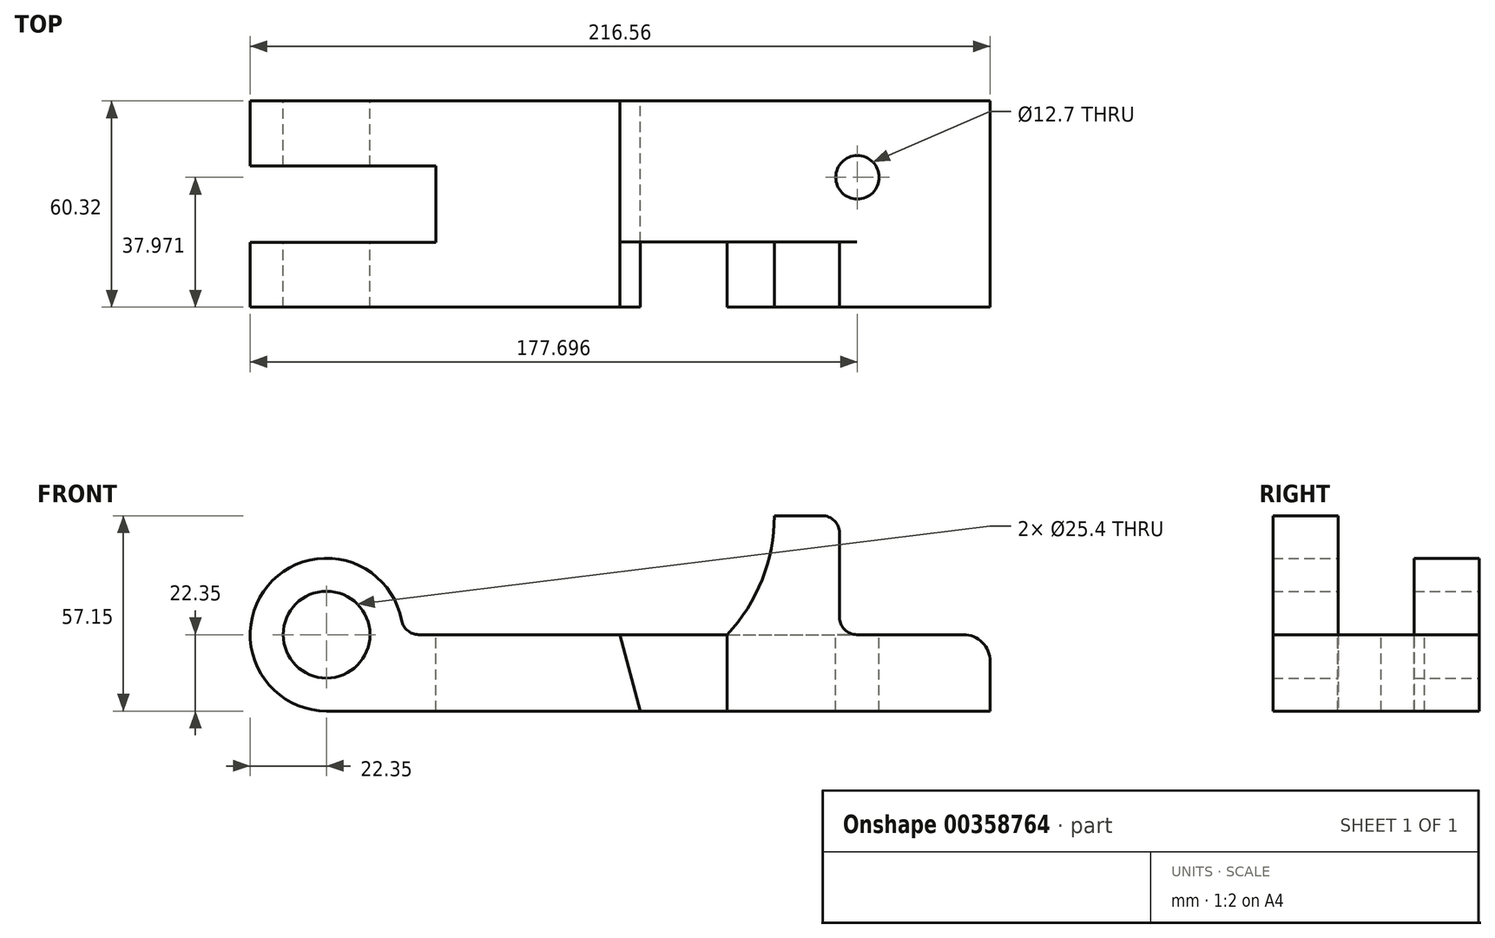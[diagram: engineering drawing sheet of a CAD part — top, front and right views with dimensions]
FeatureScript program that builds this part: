
annotation { "Feature Type Name" : "Feature", "Feature Type Description" : "" }
export const myFeature = defineFeature(function(context is Context, id is Id, definition is map)
    precondition{}
    {
        {
            var Q0;
            Q0=qCreatedBy(makeId("Front.planeOp"),FACE);
            var sketch = newSketch(context, id + "F0", { "sketchPlane" : qUnion([Q0])});
            skCircle(sketch, "E0", {"center": v(0, 0) * mm, "radius": 12.7 * mm});
            skArc(sketch, "E1", {"start": v(21.97, 4.14) * mm, "mid": v(-17.2, 14.27) * mm, "end": v(0, -22.35) * mm});
            skLineSegment(sketch, "E2", {"start": v(26.96, 0) * mm, "end": v(117.25, 0) * mm});
            skLineSegment(sketch, "E3", {"start": v(194.2, -7.87) * mm, "end": v(194.2, -22.35) * mm});
            skLineSegment(sketch, "E4", {"start": v(194.2, -22.35) * mm, "end": v(0, -22.35) * mm});
            skPoint(sketch, "E5.visualSharp", {"position": v(194.2, 0) * mm});
            skArc(sketch, "E5.filletArc", {"start": v(194.2, -7.87) * mm, "mid": v(191.9, -2.3) * mm, "end": v(186.33, 0) * mm});
            skPoint(sketch, "E6.visualSharp", {"position": v(22.35, 0) * mm});
            skArc(sketch, "E6.filletArc", {"start": v(21.97, 4.14) * mm, "mid": v(23.72, 1.17) * mm, "end": v(26.96, 0) * mm});
            skPoint(sketch, "E7", {"position": v(-22.35, 0) * mm});
            skLineSegment(sketch, "E8", {"start": v(85.85, 0) * mm, "end": v(91.85, -22.35) * mm});
            skLineSegment(sketch, "E9", {"start": v(117.25, 0) * mm, "end": v(117.25, -22.35) * mm});
            skLineSegment(sketch, "E10", {"start": v(131.04, 34.8) * mm, "end": v(145, 34.8) * mm});
            skLineSegment(sketch, "E11", {"start": v(150.09, 29.72) * mm, "end": v(150.09, 5.08) * mm});
            skArc(sketch, "E12", {"start": v(117.25, 0) * mm, "mid": v(127.46, 16.08) * mm, "end": v(131.04, 34.8) * mm});
            skLineSegment(sketch, "E13.trimOffspring", {"start": v(155.17, 0) * mm, "end": v(186.33, 0) * mm});
            skPoint(sketch, "E14.visualSharp", {"position": v(150.09, 0) * mm});
            skArc(sketch, "E14.filletArc", {"start": v(150.09, 5.08) * mm, "mid": v(151.58, 1.49) * mm, "end": v(155.17, 0) * mm});
            skPoint(sketch, "E15.visualSharp", {"position": v(150.09, 34.8) * mm});
            skArc(sketch, "E15.filletArc", {"start": v(150.09, 29.72) * mm, "mid": v(148.6, 33.31) * mm, "end": v(145, 34.8) * mm});
            skLineSegment(sketch, "E16", {"start": v(117.25, 0) * mm, "end": v(155.17, 0) * mm});
            skSolve(sketch);
        }
        {
            var Q0;
            Q0=makeQuery(id+"F0.imprint","IMPRINT",FACE,{"disambiguationData":[TD([[makeQuery(id+"F0.imprint","IMPRINT",EDGE,{"derivedFrom":sQuery(id+"F0.wireOp",EDGE,"E0")}),-1.0]])]});
            var Q1;
            {var subQ2=sQuery(id+"F0.wireOp",EDGE,"E3");Q1=makeQuery(id+"F0.imprint","IMPRINT",FACE,{"disambiguationData":[TD([[makeQuery(id+"F0.imprint","IMPRINT",EDGE,{"derivedFrom":subQ2}),-1.0]])]});}
            extrude(context, id + "F1", {"entities" : qUnion([Q0, Q1]), "endBound" : BoundingType.SYMMETRIC, "depth" : 60.32 * mm});
        }
        {
            var Q0;
            {var subQ0=sQuery(id+"F0.wireOp",EDGE,"E8");Q0=makeQuery(id+"F0.imprint","IMPRINT",FACE,{"disambiguationData":[TD([[makeQuery(id+"F0.imprint","IMPRINT",EDGE,{"derivedFrom":subQ0}),1.0]])]});}
            extrude(context, id + "F2", {"entities" : qUnion([Q0]), "oppositeDirection" : true, "depth" : 30.16 * mm});
        }
        {
            var Q0;
            {var subQ0=sQuery(id+"F0.wireOp",EDGE,"E8");Q0=makeQuery(id+"F0.imprint","IMPRINT",FACE,{"disambiguationData":[TD([[makeQuery(id+"F0.imprint","IMPRINT",EDGE,{"derivedFrom":subQ0}),1.0]])]});}
            extrude(context, id + "F3", {"entities" : qUnion([Q0]), "depth" : 11.1 * mm});
        }
        {
            var Q0;
            Q0=makeQuery(id+"F0.imprint","IMPRINT",FACE,{"disambiguationData":[TD([[makeQuery(id+"F0.imprint","IMPRINT",EDGE,{"derivedFrom":sQuery(id+"F0.wireOp",EDGE,"E10")}),-1.0]])]});
            var Q1;
            Q1=makeQuery(id+"F1.opExtrude","CAP_FACE",FACE,{"disambiguationData":[OSD([sQuery(id+"F0.wireOp",EDGE,"E3"),sQuery(id+"F0.wireOp",EDGE,"E4"),sQuery(id+"F0.wireOp",EDGE,"E5.filletArc"),sQuery(id+"F0.wireOp",EDGE,"E9"),sQuery(id+"F0.wireOp",EDGE,"E13.trimOffspring"),sQuery(id+"F0.wireOp",EDGE,"E16")])],"isStart":false});
            extrude(context, id + "F4", {"entities" : qUnion([Q0]), "operationType" : NewBodyOperationType.ADD, "endBound" : BoundingType.UP_TO_SURFACE, "endBoundEntityFace" : qUnion([Q1]), "depth" : 25.4 * mm});
        }
        {
            var Q0;
            Q0=makeQuery(id+"F0.imprint","IMPRINT",FACE,{"disambiguationData":[TD([[makeQuery(id+"F0.imprint","IMPRINT",EDGE,{"derivedFrom":sQuery(id+"F0.wireOp",EDGE,"E10")}),-1.0]])]});
            var Q1;
            Q1=makeQuery(id+"F3.opExtrude","CAP_FACE",FACE,{"disambiguationData":[OSD([sQuery(id+"F0.wireOp",EDGE,"E2"),sQuery(id+"F0.wireOp",EDGE,"E4"),sQuery(id+"F0.wireOp",EDGE,"E8"),sQuery(id+"F0.wireOp",EDGE,"E9")])],"isStart":false});
            extrude(context, id + "F5", {"entities" : qUnion([Q0]), "operationType" : NewBodyOperationType.REMOVE, "endBound" : BoundingType.UP_TO_SURFACE, "endBoundEntityFace" : qUnion([Q1]), "depth" : 25.4 * mm});
        }
        {
            var Q0;
            Q0=qCreatedBy(makeId("Top.planeOp"),FACE);
            var sketch = newSketch(context, id + "F6", { "sketchPlane" : qUnion([Q0])});
            skLineSegment(sketch, "E17", {"start": v(-22.35, 11.16) * mm, "end": v(32.04, 11.16) * mm});
            skLineSegment(sketch, "E18", {"start": v(32.04, 11.16) * mm, "end": v(32.04, -11.16) * mm});
            skLineSegment(sketch, "E19", {"start": v(32.04, -11.16) * mm, "end": v(-22.35, -11.16) * mm});
            skCircle(sketch, "E20", {"center": v(155.35, 7.81) * mm, "radius": 6.35 * mm});
            skLineSegment(sketch, "E21", {"start": v(-22.35, -11.16) * mm, "end": v(-22.35, 11.16) * mm});
            skSolve(sketch);
        }
        {
            var Q0;
            Q0=makeQuery(id+"F6.imprint","IMPRINT",FACE,{"disambiguationData":[TD([[makeQuery(id+"F6.imprint","IMPRINT",EDGE,{"derivedFrom":sQuery(id+"F6.wireOp",EDGE,"E17")}),-1.0]])]});
            extrude(context, id + "F7", {"entities" : qUnion([Q0]), "operationType" : NewBodyOperationType.REMOVE, "endBound" : BoundingType.THROUGH_ALL, "oppositeDirection" : true, "depth" : 254 * mm, "hasSecondDirection" : true, "secondDirectionBound" : SecondDirectionBoundingType.THROUGH_ALL, "secondDirectionOppositeDirection" : false, "secondDirectionDepth" : 25.4 * mm});
        }
        {
            var Q0;
            Q0=makeQuery(id+"F6.imprint","IMPRINT",FACE,{"disambiguationData":[TD([[makeQuery(id+"F6.imprint","IMPRINT",EDGE,{"derivedFrom":sQuery(id+"F6.wireOp",EDGE,"E20")}),1.0]])]});
            extrude(context, id + "F8", {"entities" : qUnion([Q0]), "operationType" : NewBodyOperationType.REMOVE, "endBound" : BoundingType.THROUGH_ALL, "oppositeDirection" : true, "depth" : 25.4 * mm});
        }
    });
